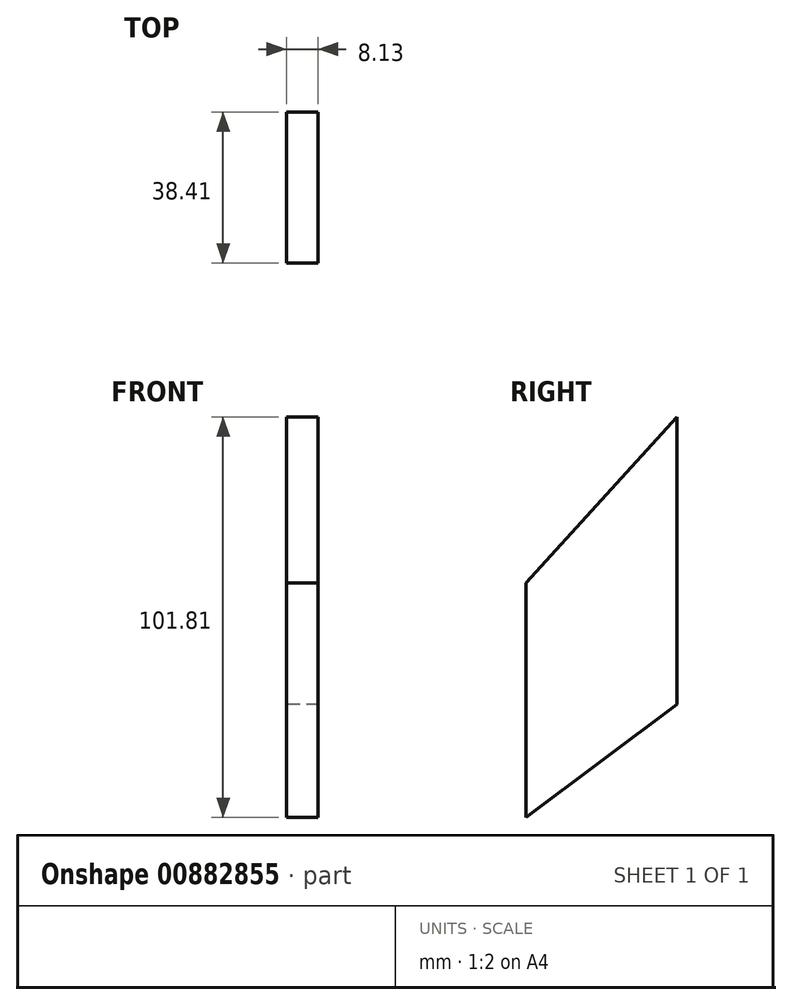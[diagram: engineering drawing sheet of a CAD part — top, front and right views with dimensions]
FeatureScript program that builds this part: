
annotation { "Feature Type Name" : "Feature", "Feature Type Description" : "" }
export const myFeature = defineFeature(function(context is Context, id is Id, definition is map)
    precondition{}
    {
        {
            var Q0;
            Q0=qCreatedBy(makeId("Right.planeOp"),FACE);
            var sketch = newSketch(context, id + "F0", { "sketchPlane" : qUnion([Q0])});
            skLineSegment(sketch, "E0", {"start": v(-23.38, -33.5) * mm, "end": v(-23.38, 26.03) * mm});
            skLineSegment(sketch, "E1", {"start": v(-23.38, 26.03) * mm, "end": v(15.03, 68.31) * mm});
            skLineSegment(sketch, "E2", {"start": v(15.03, 68.31) * mm, "end": v(15.03, -4.72) * mm});
            skLineSegment(sketch, "E3", {"start": v(15.03, -4.72) * mm, "end": v(-23.38, -33.5) * mm});
            skSolve(sketch);
        }
        {
            var Q0;
            Q0 = qSketchRegion(id + "F0", true);
            extrude(context, id + "F1", {"entities" : qUnion([Q0]), "depth" : 8.13 * mm, "offsetDistance" : 25.4 * mm});
        }
    });
